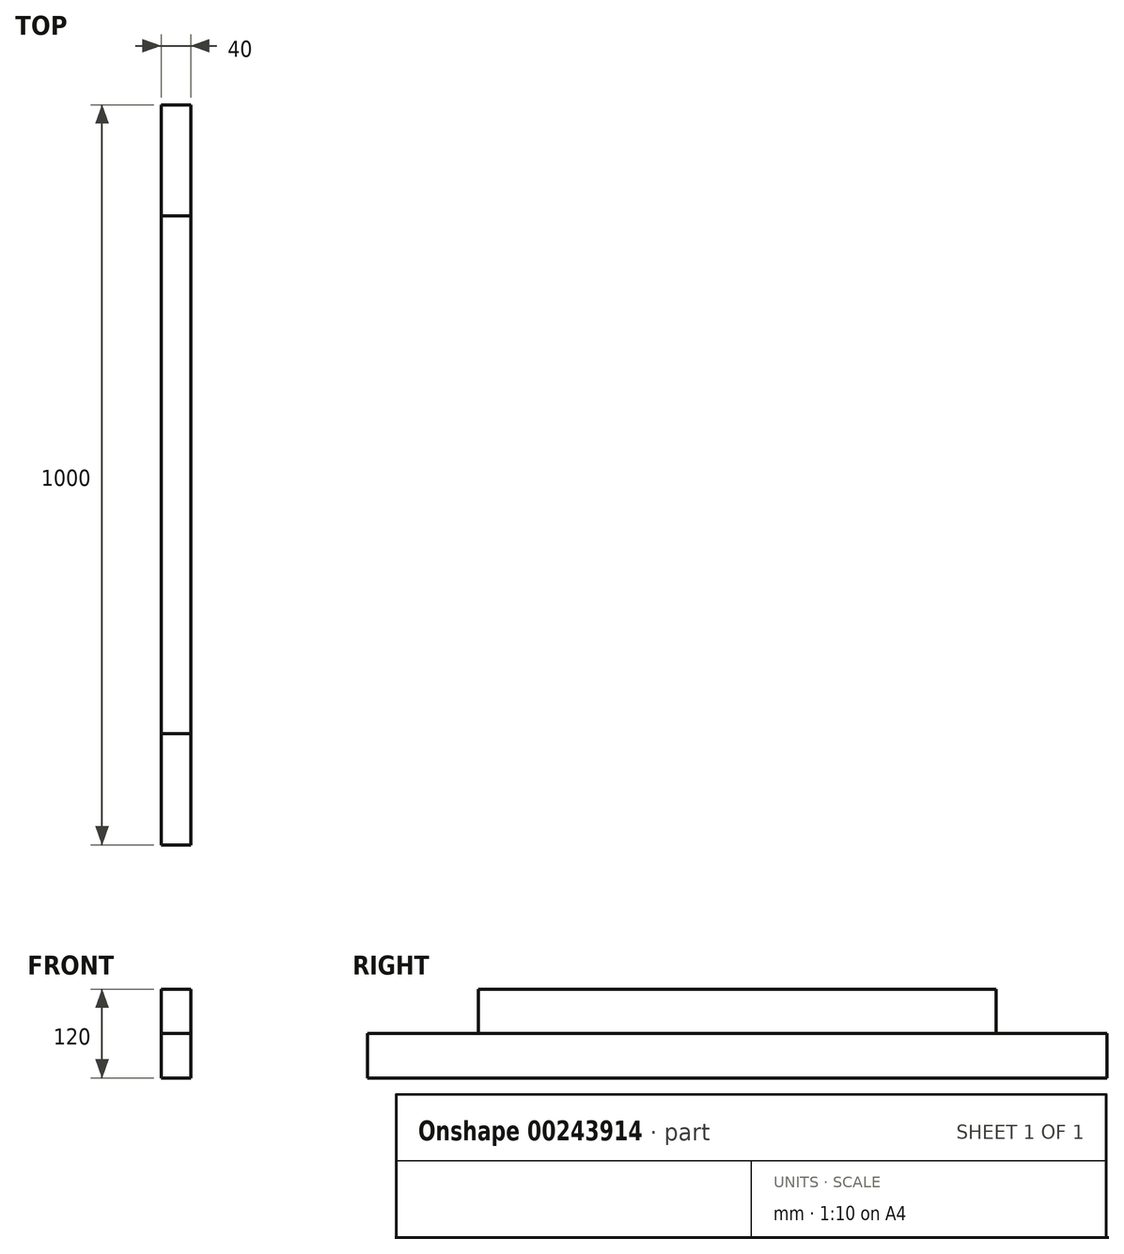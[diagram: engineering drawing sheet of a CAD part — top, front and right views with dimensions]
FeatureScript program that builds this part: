
annotation { "Feature Type Name" : "Feature", "Feature Type Description" : "" }
export const myFeature = defineFeature(function(context is Context, id is Id, definition is map)
    precondition{}
    {
        {
            var Q0;
            Q0=qCreatedBy(makeId("Top.planeOp"),FACE);
            var sketch = newSketch(context, id + "F0", { "sketchPlane" : qUnion([Q0])});
            skLineSegment(sketch, "E0.bottom", {"start": v(20, -500) * mm, "end": v(-20, -500) * mm});
            skLineSegment(sketch, "E0.top", {"start": v(20, 500) * mm, "end": v(-20, 500) * mm});
            skLineSegment(sketch, "E0.left", {"start": v(20, -500) * mm, "end": v(20, 500) * mm});
            skLineSegment(sketch, "E0.right", {"start": v(-20, -500) * mm, "end": v(-20, 500) * mm});
            skPoint(sketch, "E0.middle", {"position": v(0, 0) * mm});
            skSolve(sketch);
        }
        {
            var Q0;
            Q0=makeQuery(id+"F0.imprint","IMPRINT",FACE,{"disambiguationData":[TD([[makeQuery(id+"F0.imprint","IMPRINT",EDGE,{"derivedFrom":sQuery(id+"F0.wireOp",EDGE,"E0.bottom")}),-1.0]])]});
            extrude(context, id + "F1", {"entities" : qUnion([Q0]), "depth" : 60 * mm});
        }
        {
            var Q0;
            Q0=makeQuery(id+"F1.opExtrude","CAP_FACE",FACE,{"disambiguationData":[OSD([sQuery(id+"F0.wireOp",EDGE,"E0.bottom"),sQuery(id+"F0.wireOp",EDGE,"E0.top"),sQuery(id+"F0.wireOp",EDGE,"E0.left"),sQuery(id+"F0.wireOp",EDGE,"E0.right")])],"isStart":false});
            var sketch = newSketch(context, id + "F2", { "sketchPlane" : qUnion([Q0])});
            skLineSegment(sketch, "E1.bottom", {"start": v(20, -350) * mm, "end": v(-20, -350) * mm});
            skLineSegment(sketch, "E1.top", {"start": v(20, 350) * mm, "end": v(-20, 350) * mm});
            skLineSegment(sketch, "E1.left", {"start": v(20, -350) * mm, "end": v(20, 350) * mm});
            skLineSegment(sketch, "E1.right", {"start": v(-20, -350) * mm, "end": v(-20, 350) * mm});
            skPoint(sketch, "E1.middle", {"position": v(0, 0) * mm});
            skSolve(sketch);
        }
        {
            var Q0;
            Q0=makeQuery(id+"F2.imprint","IMPRINT",FACE,{"disambiguationData":[TD([[makeQuery(id+"F2.imprint","IMPRINT",EDGE,{"derivedFrom":sQuery(id+"F2.wireOp",EDGE,"E1.bottom")}),-1.0]])]});
            extrude(context, id + "F3", {"entities" : qUnion([Q0]), "depth" : 60 * mm});
        }
    });
